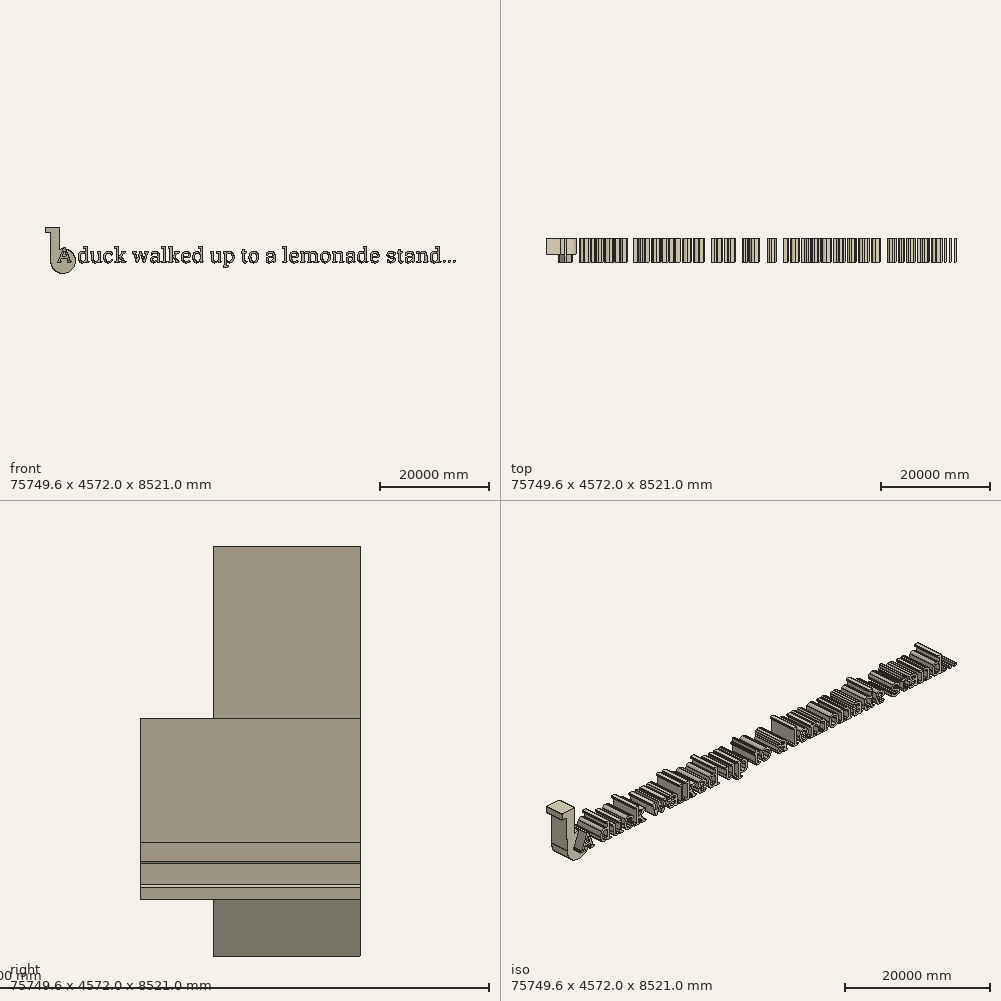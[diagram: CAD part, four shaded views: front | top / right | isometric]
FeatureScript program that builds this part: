
annotation { "Feature Type Name" : "Feature", "Feature Type Description" : "" }
export const myFeature = defineFeature(function(context is Context, id is Id, definition is map)
    precondition{}
    {
        {
            var Q0;
            Q0=qCreatedBy(makeId("Front.planeOp"),FACE);
            var sketch = newSketch(context, id + "F0", { "sketchPlane" : qUnion([Q0])});
            skText(sketch, "E0", { "text": "A duck walked up to a lemonade stand...", "fontName": "RobotoSlab-Regular.ttf"});
            const initialGuessF0  = {"E0": [-0.55567, -2.33466, 1, 0, 2.79667]};
            skSetInitialGuess(sketch, initialGuessF0);
            skSolve(sketch);
        }
        {
            var Q0;
            Q0 = qSketchRegion(id + "F0", true);
            extrude(context, id + "F1", {"entities" : qUnion([Q0]), "depth" : 4572 * mm});
        }
        {
            var Q0;
            Q0=qCreatedBy(makeId("Front.planeOp"),FACE);
            var sketch = newSketch(context, id + "F2", { "sketchPlane" : qUnion([Q0])});
            skCircle(sketch, "E1", {"center": v(632.5, -2030.4) * mm, "radius": 2286 * mm});
            skLineSegment(sketch, "E2", {"start": v(-122.67, -4188.06) * mm, "end": v(-122.67, 4204.6) * mm});
            skLineSegment(sketch, "E3", {"start": v(-122.67, 4204.6) * mm, "end": v(-2633.55, 4204.6) * mm});
            skLineSegment(sketch, "E4", {"start": v(-2633.55, 4204.6) * mm, "end": v(-2633.55, 3205.91) * mm});
            skLineSegment(sketch, "E5", {"start": v(-2633.55, 3205.91) * mm, "end": v(-1688.85, 3205.91) * mm});
            skLineSegment(sketch, "E6", {"start": v(-1688.85, 3205.91) * mm, "end": v(-1653.45, -2045.8) * mm});
            skLineSegment(sketch, "E7", {"start": v(-1653.45, -2045.8) * mm, "end": v(-122.67, -4188.06) * mm});
            skSolve(sketch);
        }
        {
            var Q0;
            {var subQ0=sQuery(id+"F2.wireOp",EDGE,"E7");Q0=makeQuery(id+"F2.imprint","IMPRINT",FACE,{"disambiguationData":[TD([[makeQuery(id+"F2.imprint","IMPRINT",EDGE,{"derivedFrom":subQ0}),1.0]])]});}
            var Q1;
            {var subQ0=sQuery(id+"F2.wireOp",EDGE,"E7");Q1=makeQuery(id+"F2.imprint","IMPRINT",FACE,{"disambiguationData":[TD([[makeQuery(id+"F2.imprint","IMPRINT",EDGE,{"derivedFrom":subQ0}),-1.0]])]});}
            var Q2;
            {var subQ0=sQuery(id+"F2.wireOp",EDGE,"E3");Q2=makeQuery(id+"F2.imprint","IMPRINT",FACE,{"disambiguationData":[TD([[makeQuery(id+"F2.imprint","IMPRINT",EDGE,{"derivedFrom":subQ0}),1.0]])]});}
            var Q3;
            {var subQ0=sQuery(id+"F2.wireOp",EDGE,"E2");var subQ1=sQuery(id+"F2.wireOp",EDGE,"E1");var subQ3=makeQuery(id+"F2.imprint","INTERSECT",VERTEX,{"derivedFrom":[subQ1,subQ0]});Q3=makeQuery(id+"F2.imprint","IMPRINT",FACE,{"disambiguationData":[TD([[makeQuery(id+"F2.imprint","IMPRINT",EDGE,{"disambiguationData":[TD([[subQ3,1.0]])],"derivedFrom":subQ1}),1.0]])]});}
            extrude(context, id + "F3", {"entities" : qUnion([Q0, Q1, Q2, Q3]), "depth" : 3048 * mm});
        }
    });
